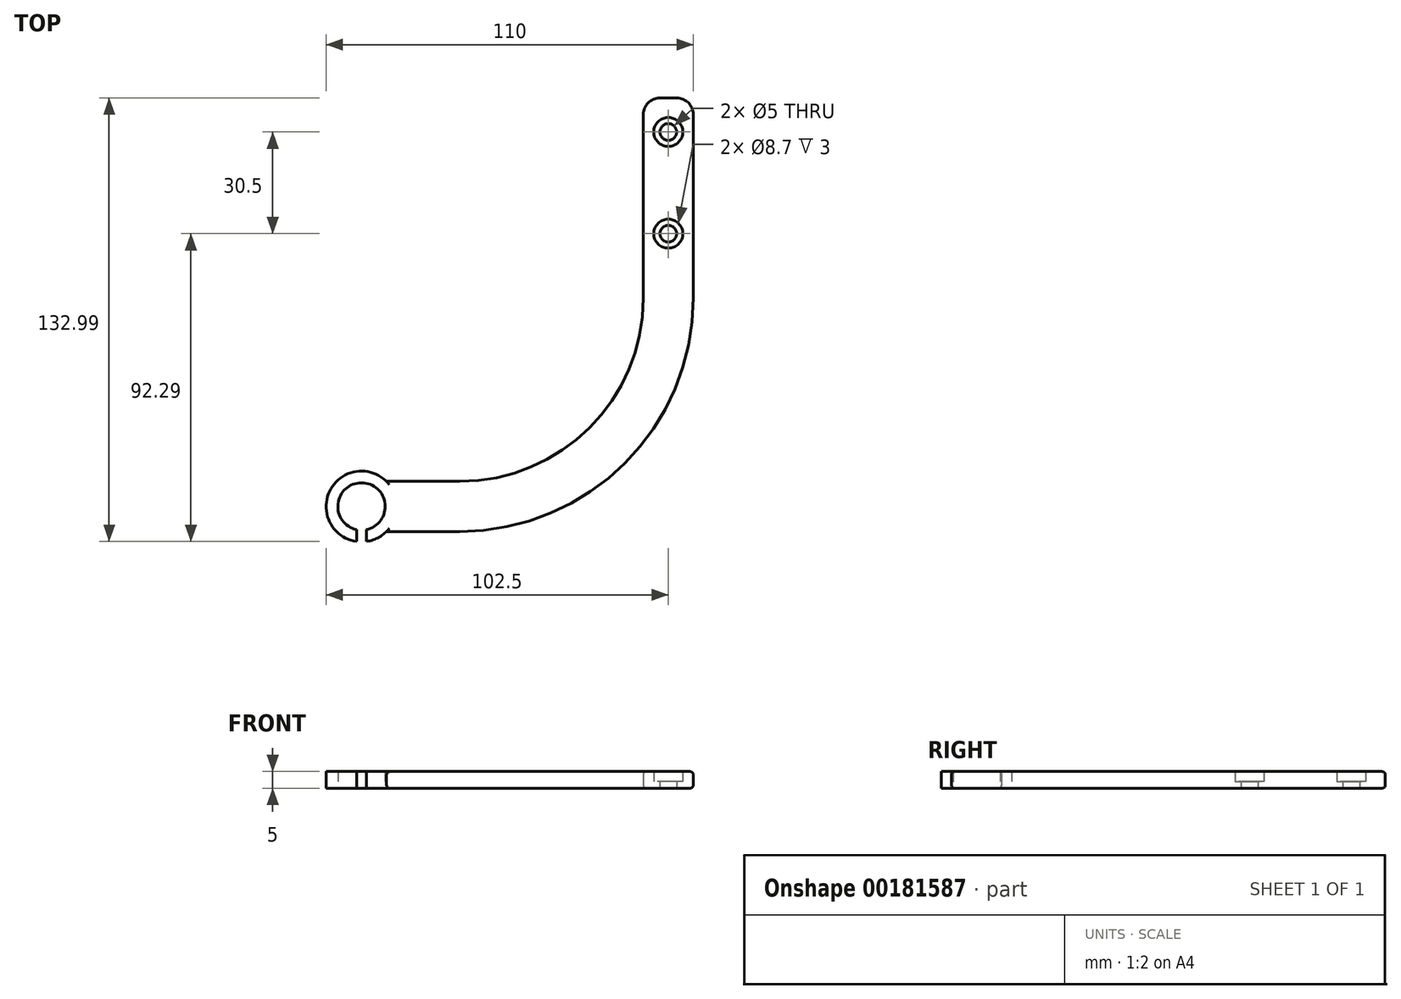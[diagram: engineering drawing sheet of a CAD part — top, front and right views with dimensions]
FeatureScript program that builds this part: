
annotation { "Feature Type Name" : "Feature", "Feature Type Description" : "" }
export const myFeature = defineFeature(function(context is Context, id is Id, definition is map)
    precondition{}
    {
        {
            var Q0;
            Q0=qCreatedBy(makeId("Top.planeOp"),FACE);
            var sketch = newSketch(context, id + "F0", { "sketchPlane" : qUnion([Q0])});
            skLineSegment(sketch, "E0.bottom", {"start": v(-15, 130) * mm, "end": v(0, 130) * mm});
            skLineSegment(sketch, "E0.left", {"start": v(-15, 130) * mm, "end": v(-15, 70) * mm});
            skLineSegment(sketch, "E0.right", {"start": v(0, 130) * mm, "end": v(0, 70) * mm});
            skArc(sketch, "E1", {"start": v(-70, 0) * mm, "mid": v(-20.5, 20.5) * mm, "end": v(0, 70) * mm});
            skArc(sketch, "E2.0", {"start": v(-70, 15) * mm, "mid": v(-31.1, 31.1) * mm, "end": v(-15, 70) * mm});
            skLineSegment(sketch, "E3.bottom", {"start": v(-91.9, 15) * mm, "end": v(-70, 15) * mm});
            skLineSegment(sketch, "E3.top", {"start": v(-91.9, 0) * mm, "end": v(-70, 0) * mm});
            skLineSegment(sketch, "E3.left", {"start": v(-91.9, 15) * mm, "end": v(-91.9, 0) * mm, "construction": true});
            skArc(sketch, "E4", {"start": v(-97.9, -3) * mm, "mid": v(-94.66, -1.98) * mm, "end": v(-91.9, 0) * mm});
            skArc(sketch, "E5.0", {"start": v(-97.9, 0.56) * mm, "mid": v(-99.4, 14.6) * mm, "end": v(-100.9, 0.56) * mm});
            skPoint(sketch, "E6", {"position": v(-91.9, 7.5) * mm});
            skLineSegment(sketch, "E7", {"start": v(0, 70) * mm, "end": v(0, 0) * mm, "construction": true});
            skLineSegment(sketch, "E8", {"start": v(-100.9, 0.56) * mm, "end": v(-100.9, -3) * mm});
            skLineSegment(sketch, "E9", {"start": v(-97.9, 0.56) * mm, "end": v(-97.9, -3) * mm});
            skArc(sketch, "E10.trimOffspring", {"start": v(-91.9, 15) * mm, "mid": v(-108.88, 12.24) * mm, "end": v(-100.9, -3) * mm});
            skLineSegment(sketch, "E11", {"start": v(-100.9, 0.56) * mm, "end": v(-97.9, 0.56) * mm, "construction": true});
            skPoint(sketch, "E12", {"position": v(-99.4, 0.56) * mm});
            skCircle(sketch, "E13", {"center": v(-7.5, 119.8) * mm, "radius": 2.5 * mm});
            skCircle(sketch, "E14", {"center": v(-7.5, 89.3) * mm, "radius": 2.5 * mm});
            skLineSegment(sketch, "E15", {"start": v(-15, 70) * mm, "end": v(0, 70) * mm, "construction": true});
            skPoint(sketch, "E16", {"position": v(-7.5, 70) * mm});
            skSolve(sketch);
        }
        {
            var Q0;
            Q0 = qSketchRegion(id + "F0", true);
            extrude(context, id + "F1", {"entities" : qUnion([Q0]), "depth" : 5 * mm});
        }
        {
            var Q0;
            Q0=qCreatedBy(makeId("Top.planeOp"),FACE);
            cPlane(context, id + "F2", {"entities" : qUnion([Q0]), "cplaneType" : CPlaneType.OFFSET, "offset" : 2 * mm, "width" : 150 * mm, "height" : 150 * mm});
        }
        {
            var Q0;
            Q0=qCreatedBy(id+"F2.planeOp",FACE);
            var sketch = newSketch(context, id + "F3", { "sketchPlane" : qUnion([Q0])});
            skCircle(sketch, "E17", {"center": v(-7.5, 89.3) * mm, "radius": 4.35 * mm});
            skCircle(sketch, "E18", {"center": v(-7.5, 119.8) * mm, "radius": 4.35 * mm});
            skSolve(sketch);
        }
        {
            var Q0;
            Q0 = qSketchRegion(id + "F3", true);
            var Q1;
            Q1=makeQuery(id+"F1.opExtrude","CAP_FACE",FACE,{"disambiguationData":[OSD([sQuery(id+"F0.wireOp",EDGE,"E0.bottom"),sQuery(id+"F0.wireOp",EDGE,"E0.left"),sQuery(id+"F0.wireOp",EDGE,"E0.right"),sQuery(id+"F0.wireOp",EDGE,"E1"),sQuery(id+"F0.wireOp",EDGE,"E2.0"),sQuery(id+"F0.wireOp",EDGE,"E3.bottom"),sQuery(id+"F0.wireOp",EDGE,"E3.top"),sQuery(id+"F0.wireOp",EDGE,"E4"),sQuery(id+"F0.wireOp",EDGE,"E5.0"),sQuery(id+"F0.wireOp",EDGE,"E8"),sQuery(id+"F0.wireOp",EDGE,"E9"),sQuery(id+"F0.wireOp",EDGE,"E10.trimOffspring"),sQuery(id+"F0.wireOp",EDGE,"E13"),sQuery(id+"F0.wireOp",EDGE,"E14")])],"isStart":false});
            extrude(context, id + "F4", {"entities" : qUnion([Q0]), "operationType" : NewBodyOperationType.REMOVE, "endBound" : BoundingType.UP_TO_SURFACE, "endBoundEntityFace" : qUnion([Q1]), "depth" : 25 * mm});
        }
        {
            var Q0;
            Q0=makeQuery(id+"F1.opExtrude","SWEPT_EDGE",EDGE,{"disambiguationData":[OSD([sQuery(id+"F0.wireOp",EDGE,"E0.bottom"),sQuery(id+"F0.wireOp",EDGE,"E0.right")])]});
            fillet(context, id + "F5", {"entities" : qUnion([Q0]), "radius" : 5 * mm, "tangentPropagation" : true, "allowEdgeOverflow" : false});
        }
        {
            var Q0;
            Q0=makeQuery(id+"F1.opExtrude","SWEPT_EDGE",EDGE,{"disambiguationData":[OSD([sQuery(id+"F0.wireOp",EDGE,"E0.bottom"),sQuery(id+"F0.wireOp",EDGE,"E0.left")])]});
            fillet(context, id + "F6", {"entities" : qUnion([Q0]), "radius" : 5 * mm, "tangentPropagation" : true, "allowEdgeOverflow" : false});
        }
        {
            var Q0;
            Q0=makeQuery(id+"F1.opExtrude","CAP_EDGE",EDGE,{"disambiguationData":[OSD([sQuery(id+"F0.wireOp",EDGE,"E0.right")])],"isStart":false});
            fillet(context, id + "F7", {"entities" : qUnion([Q0]), "radius" : 1 * mm, "tangentPropagation" : true, "allowEdgeOverflow" : false});
        }
        {
            var Q0;
            Q0=makeQuery(id+"F1.opExtrude","CAP_EDGE",EDGE,{"disambiguationData":[OSD([sQuery(id+"F0.wireOp",EDGE,"E0.right")])],"isStart":true});
            fillet(context, id + "F8", {"entities" : qUnion([Q0]), "radius" : 1 * mm, "tangentPropagation" : true, "allowEdgeOverflow" : false});
        }
    });
